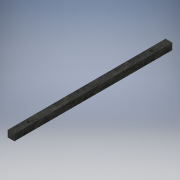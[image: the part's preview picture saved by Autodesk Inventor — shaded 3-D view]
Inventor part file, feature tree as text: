
AUTODESK INVENTOR PART (.ipt)
format: ipt  version: 2019 (Build 230136000, 136)  size: 115,200 bytes
history: native  units: mm
features: extrude x2, sketch x2
ambient origin geometry x8: Origin, YZ Plane, XZ Plane, XY Plane, X Axis, Y Axis, Z Axis, Center Point
bodies: Solid1 (feature_tree)
feature tree (4):
  extrude  "Extrusion1"  Depth=460.0mm
  extrude  "Extrusion2"  Depth=213.727452mm
  sketch  "Sketch1"  dims[d0=19.0mm d1=460.0mm]
  sketch  "Sketch2"  dims[d2=19.0mm d3=213.727452mm d4=19.0mm d5=0.0mm d6=50.0mm d7=50.0mm d8=9.5mm d9=9.5mm d10=8.0mm d11=8.0mm d12=19.0mm d13=0.0mm]
